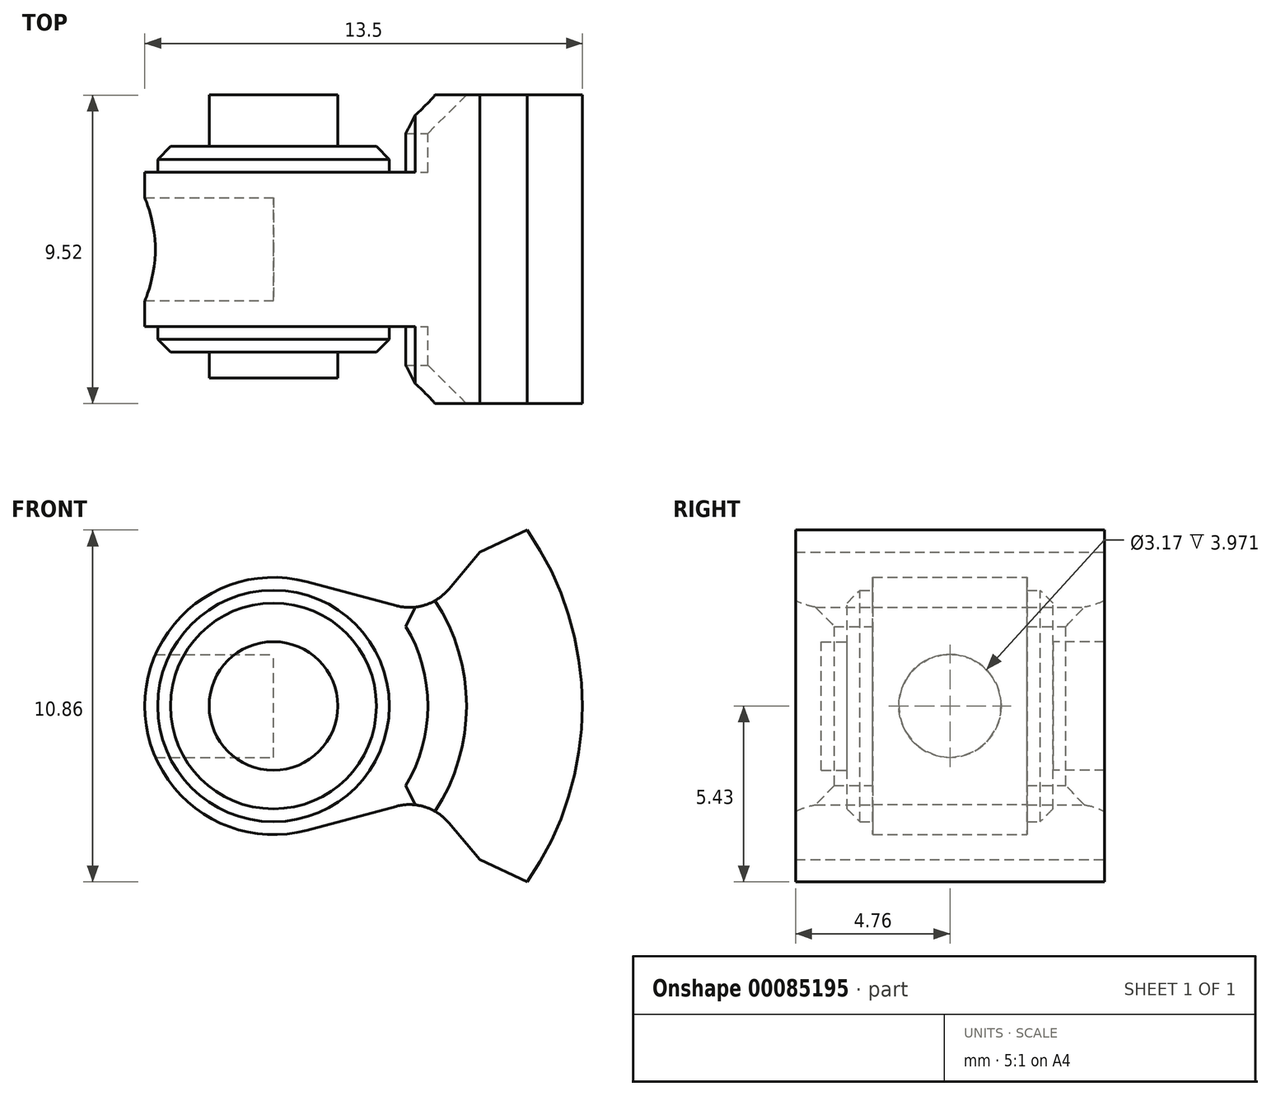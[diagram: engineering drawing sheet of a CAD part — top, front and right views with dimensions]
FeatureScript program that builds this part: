
annotation { "Feature Type Name" : "Feature", "Feature Type Description" : "" }
export const myFeature = defineFeature(function(context is Context, id is Id, definition is map)
    precondition{}
    {
        {
            var Q0;
            Q0=qCreatedBy(makeId("Front.planeOp"),FACE);
            var sketch = newSketch(context, id + "F0", { "sketchPlane" : qUnion([Q0])});
            skCircle(sketch, "E0", {"center": v(0, 0) * mm, "radius": 3.97 * mm});
            skCircle(sketch, "E1", {"center": v(0, 0) * mm, "radius": 3.57 * mm});
            skArc(sketch, "E2", {"start": v(7.83, -5.43) * mm, "mid": v(9.53, 0) * mm, "end": v(7.83, 5.43) * mm});
            skArc(sketch, "E3", {"start": v(6.36, -4.75) * mm, "mid": v(7.94, 0) * mm, "end": v(6.36, 4.75) * mm, "construction": true});
            skLineSegment(sketch, "E4", {"start": v(0, 0) * mm, "end": v(26.57, 0) * mm, "construction": true});
            skLineSegment(sketch, "E5", {"start": v(2.38, 0) * mm, "end": v(2.38, -12.57) * mm, "construction": true});
            skLineSegment(sketch, "E6", {"start": v(4.76, -2.83) * mm, "end": v(6.36, -4.75) * mm});
            skArc(sketch, "E7", {"start": v(3.57, -3.15) * mm, "mid": v(4.76, 0) * mm, "end": v(3.57, 3.15) * mm});
            skLineSegment(sketch, "E8", {"start": v(0, 0) * mm, "end": v(-17.39, 0) * mm, "construction": true});
            skLineSegment(sketch, "E9", {"start": v(4.76, 2.83) * mm, "end": v(1.03, 3.83) * mm});
            skLineSegment(sketch, "E10", {"start": v(4.76, -2.83) * mm, "end": v(1.03, -3.83) * mm});
            skLineSegment(sketch, "E11.trimOffspring", {"start": v(4.76, 2.83) * mm, "end": v(6.36, 4.75) * mm});
            skLineSegment(sketch, "E12", {"start": v(6.36, 4.75) * mm, "end": v(7.83, 5.43) * mm});
            skLineSegment(sketch, "E13", {"start": v(6.36, -4.75) * mm, "end": v(7.83, -5.43) * mm});
            skSolve(sketch);
        }
        {
            var Q0;
            Q0=makeQuery(id+"F0.imprint","IMPRINT",FACE,{"disambiguationData":[TD([[makeQuery(id+"F0.imprint","IMPRINT",EDGE,{"derivedFrom":sQuery(id+"F0.wireOp",EDGE,"E2")}),1.0]])]});
            extrude(context, id + "F1", {"entities" : qUnion([Q0]), "depth" : 4.76 * mm, "hasSecondDirection" : true, "secondDirectionOppositeDirection" : true, "secondDirectionDepth" : 4.76 * mm});
        }
        {
            var Q0;
            {var subQ5=sQuery(id+"F0.wireOp",EDGE,"E7");Q0=makeQuery(id+"F0.imprint","IMPRINT",FACE,{"disambiguationData":[TD([[makeQuery(id+"F0.imprint","IMPRINT",EDGE,{"derivedFrom":subQ5}),1.0]])]});}
            extrude(context, id + "F2", {"entities" : qUnion([Q0]), "operationType" : NewBodyOperationType.ADD, "depth" : 2.38 * mm, "hasSecondDirection" : true, "secondDirectionOppositeDirection" : true, "secondDirectionDepth" : 2.38 * mm});
        }
        {
            var Q0;
            Q0=makeQuery(id+"F0.imprint","IMPRINT",FACE,{"disambiguationData":[TD([[makeQuery(id+"F0.imprint","IMPRINT",EDGE,{"derivedFrom":sQuery(id+"F0.wireOp",EDGE,"E1")}),-1.0]])]});
            extrude(context, id + "F3", {"entities" : qUnion([Q0]), "operationType" : NewBodyOperationType.ADD, "depth" : 2.38 * mm, "hasSecondDirection" : true, "secondDirectionOppositeDirection" : true, "secondDirectionDepth" : 2.38 * mm});
        }
        {
            var Q0;
            Q0=makeQuery(id+"F0.imprint","IMPRINT",FACE,{"disambiguationData":[TD([[makeQuery(id+"F0.imprint","IMPRINT",EDGE,{"derivedFrom":sQuery(id+"F0.wireOp",EDGE,"E1")}),1.0]])]});
            extrude(context, id + "F4", {"entities" : qUnion([Q0]), "operationType" : NewBodyOperationType.ADD, "depth" : 3.17 * mm, "hasSecondDirection" : true, "secondDirectionOppositeDirection" : true, "secondDirectionDepth" : 3.17 * mm});
        }
        {
            var Q0;
            Q0=makeQuery(id+"F4.opExtrude","CAP_FACE",FACE,{"disambiguationData":[OSD([sQuery(id+"F0.wireOp",EDGE,"E1")])],"isStart":false});
            var sketch = newSketch(context, id + "F5", { "sketchPlane" : qUnion([Q0])});
            skCircle(sketch, "E14", {"center": v(0, 0) * mm, "radius": 1.98 * mm});
            skSolve(sketch);
        }
        {
            var Q0;
            Q0 = qSketchRegion(id + "F5", true);
            extrude(context, id + "F6", {"entities" : qUnion([Q0]), "operationType" : NewBodyOperationType.ADD, "depth" : 0.8 * mm});
        }
        {
            var Q0;
            Q0=makeQuery(id+"F4.opExtrude","CAP_FACE",FACE,{"disambiguationData":[OSD([sQuery(id+"F0.wireOp",EDGE,"E1")])],"isStart":true});
            var sketch = newSketch(context, id + "F7", { "sketchPlane" : qUnion([Q0])});
            skCircle(sketch, "E15", {"center": v(0, 0) * mm, "radius": 1.98 * mm});
            skSolve(sketch);
        }
        {
            var Q0;
            Q0 = qSketchRegion(id + "F7", true);
            extrude(context, id + "F8", {"entities" : qUnion([Q0]), "operationType" : NewBodyOperationType.ADD, "depth" : 1.59 * mm});
        }
        {
            var Q0;
            Q0=makeQuery(id+"F1.opExtrude","SWEPT_EDGE",EDGE,{"disambiguationData":[OSD([sQuery(id+"F0.wireOp",EDGE,"E6"),sQuery(id+"F0.wireOp",EDGE,"E10")])]});
            var Q1;
            Q1=makeQuery(id+"F1.opExtrude","SWEPT_EDGE",EDGE,{"disambiguationData":[OSD([sQuery(id+"F0.wireOp",EDGE,"E9"),sQuery(id+"F0.wireOp",EDGE,"E11.trimOffspring")])]});
            fillet(context, id + "F9", {"entities" : qUnion([Q0, Q1]), "radius" : 1.59 * mm, "tangentPropagation" : true, "allowEdgeOverflow" : false});
        }
        {
            var Q0;
            Q0=makeQuery(id+"F1.opExtrude","CAP_EDGE",EDGE,{"disambiguationData":[OSD([sQuery(id+"F0.wireOp",EDGE,"E7")])],"isStart":false});
            var Q1;
            Q1=makeQuery(id+"F1.opExtrude","CAP_EDGE",EDGE,{"disambiguationData":[OSD([sQuery(id+"F0.wireOp",EDGE,"E7")])],"isStart":true});
            chamfer(context, id + "F10", {"entities" : qUnion([Q0, Q1]), "width" : 1.2 * mm, "tangentPropagation" : true});
        }
        {
            var Q0;
            Q0=makeQuery(id+"F4.opExtrude","CAP_EDGE",EDGE,{"disambiguationData":[OSD([sQuery(id+"F0.wireOp",EDGE,"E1")])],"isStart":false});
            var Q1;
            Q1=makeQuery(id+"F4.opExtrude","CAP_EDGE",EDGE,{"disambiguationData":[OSD([sQuery(id+"F0.wireOp",EDGE,"E1")])],"isStart":true});
            chamfer(context, id + "F11", {"entities" : qUnion([Q0, Q1]), "width" : 0.4 * mm, "tangentPropagation" : true});
        }
        {
            var Q0;
            {var subQ0=sQuery(id+"F0.wireOp",EDGE,"E10");var subQ1=sQuery(id+"F0.wireOp",EDGE,"E9");var subQ2=sQuery(id+"F0.wireOp",EDGE,"E7");Q0=makeQuery(id+"F2.boolean.opBoolean","SPLIT",EDGE,{"disambiguationData":[TD([makeQuery(id+"F2.opExtrude","CAP_FACE",FACE,{"disambiguationData":[OSD([sQuery(id+"F0.wireOp",EDGE,"E0"),subQ2,subQ1,subQ0])],"isStart":false})])],"derivedFrom":makeQuery(id+"F1.opExtrude","SWEPT_EDGE",EDGE,{"disambiguationData":[OSD([subQ2,subQ0])]})});}
            var Q1;
            {var subQ0=sQuery(id+"F0.wireOp",EDGE,"E10");var subQ1=sQuery(id+"F0.wireOp",EDGE,"E9");var subQ2=sQuery(id+"F0.wireOp",EDGE,"E7");Q1=makeQuery(id+"F2.boolean.opBoolean","SPLIT",EDGE,{"disambiguationData":[TD([makeQuery(id+"F2.opExtrude","CAP_FACE",FACE,{"disambiguationData":[OSD([sQuery(id+"F0.wireOp",EDGE,"E0"),subQ2,subQ1,subQ0])],"isStart":false})])],"derivedFrom":makeQuery(id+"F1.opExtrude","SWEPT_EDGE",EDGE,{"disambiguationData":[OSD([subQ2,subQ1])]})});}
            var Q2;
            {var subQ0=sQuery(id+"F0.wireOp",EDGE,"E10");var subQ1=sQuery(id+"F0.wireOp",EDGE,"E9");var subQ2=sQuery(id+"F0.wireOp",EDGE,"E7");Q2=makeQuery(id+"F2.boolean.opBoolean","SPLIT",EDGE,{"disambiguationData":[TD([makeQuery(id+"F2.opExtrude","CAP_FACE",FACE,{"disambiguationData":[OSD([sQuery(id+"F0.wireOp",EDGE,"E0"),subQ2,subQ1,subQ0])],"isStart":true})])],"derivedFrom":makeQuery(id+"F1.opExtrude","SWEPT_EDGE",EDGE,{"disambiguationData":[OSD([subQ2,subQ0])]})});}
            var Q3;
            {var subQ0=sQuery(id+"F0.wireOp",EDGE,"E10");var subQ1=sQuery(id+"F0.wireOp",EDGE,"E9");var subQ2=sQuery(id+"F0.wireOp",EDGE,"E7");Q3=makeQuery(id+"F2.boolean.opBoolean","SPLIT",EDGE,{"disambiguationData":[TD([makeQuery(id+"F2.opExtrude","CAP_FACE",FACE,{"disambiguationData":[OSD([sQuery(id+"F0.wireOp",EDGE,"E0"),subQ2,subQ1,subQ0])],"isStart":true})])],"derivedFrom":makeQuery(id+"F1.opExtrude","SWEPT_EDGE",EDGE,{"disambiguationData":[OSD([subQ2,subQ1])]})});}
            chamfer(context, id + "F12", {"entities" : qUnion([Q0, Q1, Q2, Q3]), "width" : 0.4 * mm, "tangentPropagation" : true});
        }
        {
            var Q0;
            Q0=qCreatedBy(makeId("Right.planeOp"),FACE);
            var sketch = newSketch(context, id + "F13", { "sketchPlane" : qUnion([Q0])});
            skCircle(sketch, "E16", {"center": v(0, 0) * mm, "radius": 1.59 * mm});
            skSolve(sketch);
        }
        {
            var Q0;
            Q0=makeQuery(id+"F13.imprint","IMPRINT",FACE,{"disambiguationData":[TD([[makeQuery(id+"F13.imprint","IMPRINT",EDGE,{"derivedFrom":sQuery(id+"F13.wireOp",EDGE,"E16")}),1.0]])]});
            extrude(context, id + "F14", {"entities" : qUnion([Q0]), "operationType" : NewBodyOperationType.REMOVE, "oppositeDirection" : true, "depth" : 5.2 * mm});
        }
    });
